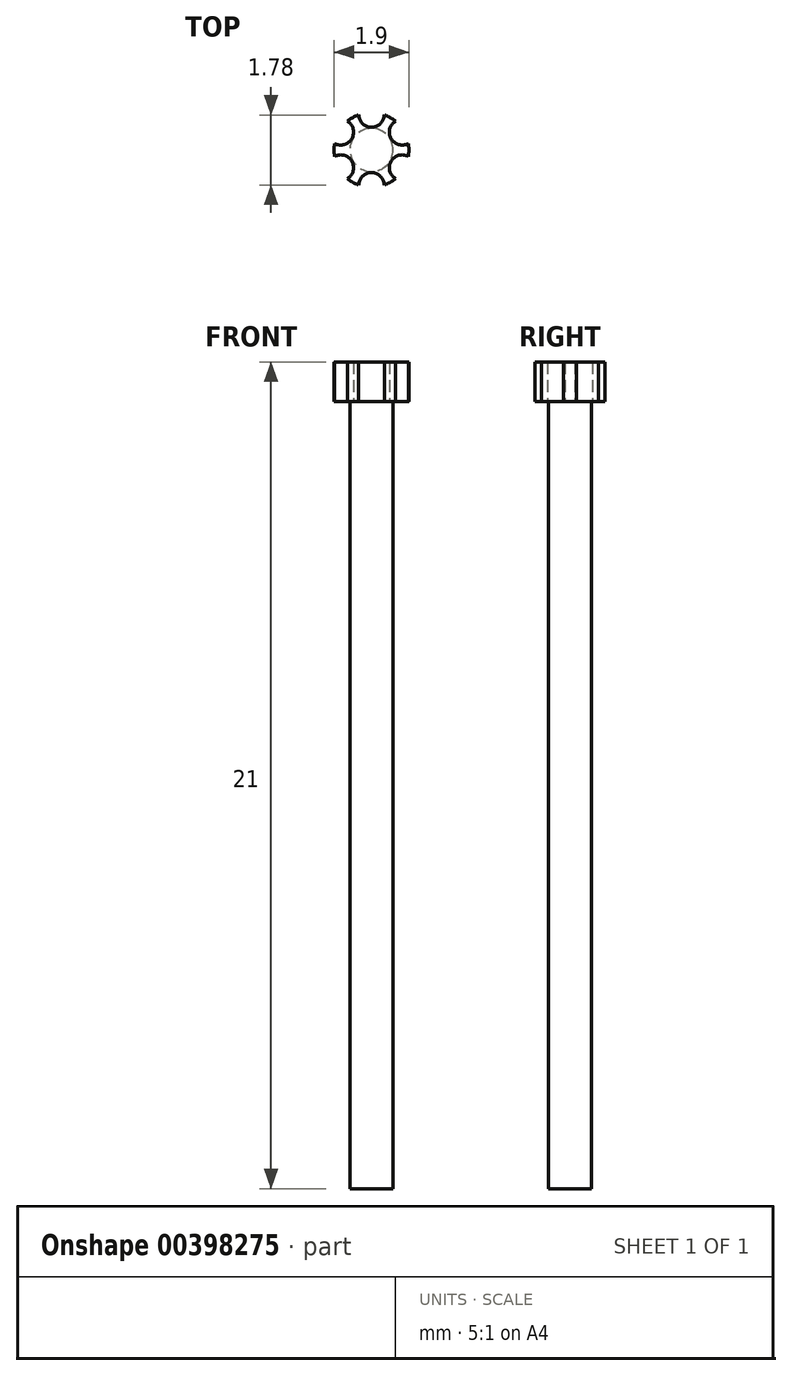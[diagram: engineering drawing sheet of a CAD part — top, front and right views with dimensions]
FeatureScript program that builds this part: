
annotation { "Feature Type Name" : "Feature", "Feature Type Description" : "" }
export const myFeature = defineFeature(function(context is Context, id is Id, definition is map)
    precondition{}
    {
        {
            var Q0;
            Q0=qCreatedBy(makeId("Top.planeOp"),FACE);
            var sketch = newSketch(context, id + "F0", { "sketchPlane" : qUnion([Q0])});
            skArc(sketch, "E0", {"start": v(-0.32, 0.9) * mm, "mid": v(-0.48, 0.82) * mm, "end": v(-0.61, 0.73) * mm});
            skCircle(sketch, "E1", {"center": v(0, 0) * mm, "radius": 0.9 * mm, "construction": true});
            skLineSegment(sketch, "E2", {"start": v(-1.28, 0.74) * mm, "end": v(1.78, -1.03) * mm, "construction": true});
            skLineSegment(sketch, "E3", {"start": v(1.14, 0.66) * mm, "end": v(-1.2, -0.69) * mm, "construction": true});
            skLineSegment(sketch, "E4", {"start": v(0, 1.42) * mm, "end": v(0, -1.26) * mm, "construction": true});
            skArc(sketch, "E5", {"start": v(-0.32, 0.9) * mm, "mid": v(0, 0.58) * mm, "end": v(0.32, 0.9) * mm});
            skArc(sketch, "E6", {"start": v(-0.94, 0.16) * mm, "mid": v(-0.5, 0.29) * mm, "end": v(-0.61, 0.73) * mm});
            skArc(sketch, "E7", {"start": v(-0.61, -0.73) * mm, "mid": v(-0.5, -0.29) * mm, "end": v(-0.94, -0.16) * mm});
            skArc(sketch, "E8", {"start": v(0.32, -0.9) * mm, "mid": v(0, -0.57) * mm, "end": v(-0.32, -0.9) * mm});
            skArc(sketch, "E9", {"start": v(0.94, -0.16) * mm, "mid": v(0.5, -0.29) * mm, "end": v(0.61, -0.73) * mm});
            skArc(sketch, "E10", {"start": v(0.61, 0.73) * mm, "mid": v(0.5, 0.29) * mm, "end": v(0.94, 0.16) * mm});
            skArc(sketch, "E11.trimOffspring", {"start": v(0.61, 0.73) * mm, "mid": v(0.47, 0.82) * mm, "end": v(0.32, 0.9) * mm});
            skArc(sketch, "E12.trimOffspring", {"start": v(0.94, -0.16) * mm, "mid": v(0.95, 0) * mm, "end": v(0.94, 0.16) * mm});
            skArc(sketch, "E13.trimOffspring", {"start": v(0.32, -0.9) * mm, "mid": v(0.48, -0.82) * mm, "end": v(0.61, -0.73) * mm});
            skArc(sketch, "E14.trimOffspring", {"start": v(-0.61, -0.73) * mm, "mid": v(-0.47, -0.82) * mm, "end": v(-0.32, -0.9) * mm});
            skArc(sketch, "E15.trimOffspring", {"start": v(-0.94, 0.16) * mm, "mid": v(-0.95, 0) * mm, "end": v(-0.94, -0.16) * mm});
            skSolve(sketch);
        }
        {
            var Q0;
            Q0 = qSketchRegion(id + "F0", true);
            extrude(context, id + "F1", {"entities" : qUnion([Q0]), "depth" : 1 * mm});
        }
        {
            var Q0;
            Q0=qCreatedBy(makeId("Top.planeOp"),FACE);
            var sketch = newSketch(context, id + "F2", { "sketchPlane" : qUnion([Q0])});
            skCircle(sketch, "E16", {"center": v(0, 0) * mm, "radius": 0.55 * mm});
            skSolve(sketch);
        }
        {
            var Q0;
            Q0 = qSketchRegion(id + "F2", true);
            extrude(context, id + "F3", {"entities" : qUnion([Q0]), "operationType" : NewBodyOperationType.ADD, "oppositeDirection" : true, "depth" : 20 * mm});
        }
    });
